# Revit family: Plumbing_Joints_Aignep_Analogue-Timer-Din43650A-90985
name_source: partatom
category: Pipe Accessories
revit_build: Autodesk Revit 2018 (Build: 20170223_1515(x64)
units: mm (PartAtom-declared; Revit-internal decimal feet)

## family parameters
Always vertical = Yes
Cut with Voids When Loaded = No
OmniClass Number = 23.27.43.00
OmniClass Title = Pipe Fittings
Part Type = Valve - Breaks Into
Round Connector Dimension = Use Diameter
Shared = No
Work Plane-Based = No

## types (1)
- 90985
    Apparent Load = 0 VA
    Assembly Code = D2040100
    BIMobject category = Valves
    Description = Analogue timer DIN43650A
    Design country = Italy
    Edition number = 1
    Frequency = 60 Hz
    IFC Classification = Pipe Fitting
    Keynote = 15410
    Manufacturer = Aignep Spa
    Manufacturer country = Italy
    Manufacturer name = Aignep Spa
    Material main = Brass
    Model = 90985
    OmniClass Code = 23-27 43 00
    OmniClass Description = Pipe Fittings
    Product Guid = 00cd7a62-7d46-45d0-990b-e35a94039c58
    Product Material = AIGNEP - Plastic - Black
    Product SKU = Analogue-Timer-Din43650A-90985
    Product certification = https://www.aignep.com
    Product data url = https://www.bimobject.com
    Product family = INFINITY
    Product group = Valves
    Product name = Analogue Timer Din43650A - 90985
    Product url = https://www.aignep.com
    QR code = https://www.bimobject.com
    Temperature Range = from - 10 °C to + 50 °C
    URL = https://www.aignep.com
    Voltage = 24 V

## geometry (parser evidence)
native form markers: Sweep x1
no freeform markers — native parametric forms only
